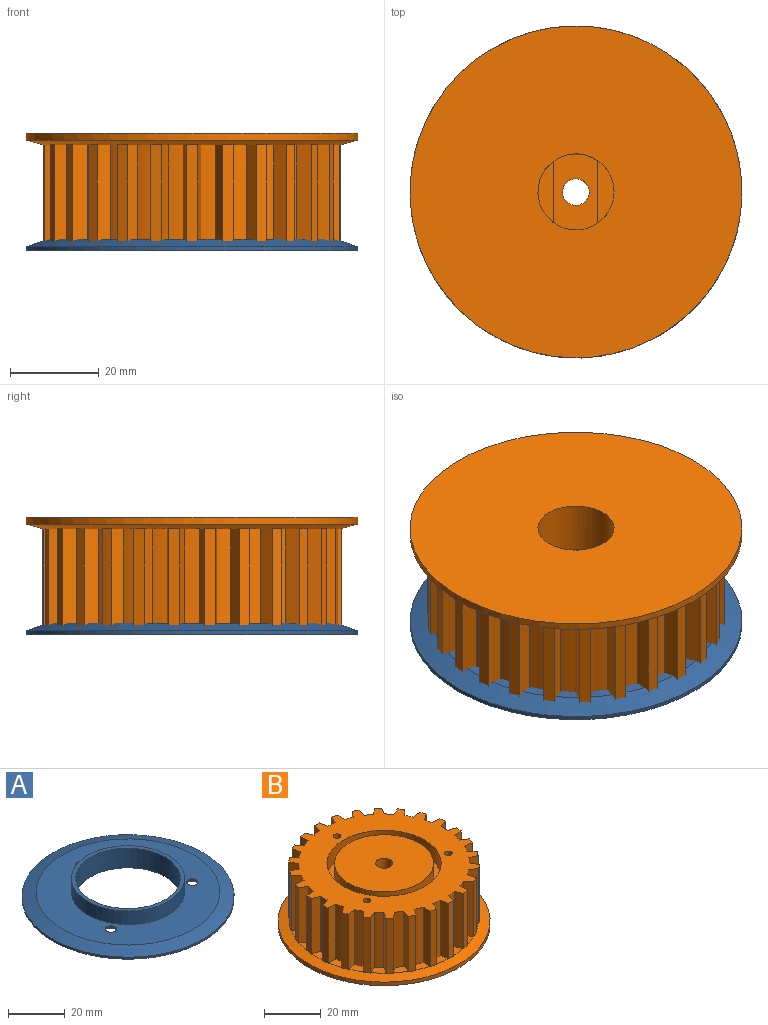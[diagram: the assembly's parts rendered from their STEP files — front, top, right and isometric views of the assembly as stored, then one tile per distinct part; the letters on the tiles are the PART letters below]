
ASSEMBLY  parts=2 mates=1
PART A: 13 faces, bbox 75x75x8.5 mm
  f0: cylinder r=2mm len=4mm, axis (0,0,-1), area 7.5mm2, adj f4,f9
  f1: cylinder r=2mm len=4mm, axis (0,0,-1), area 7.5mm2, adj f4,f11
  f2: cylinder r=2mm len=4mm, axis (0,0,-1), area 7.5mm2, adj f4,f10
  f3: cylinder r=37.5mm len=75mm, axis (0,0,-1), area 207mm2, adj f5,f12
  f4: plane 65x65mm, normal (0,0,1), area 2024mm2, adj f0,f1,f2,f7,f12
  f5: plane 75x75mm, normal (0,0,-1), area 3191.9mm2, adj f3,f6,f9,f10,f11
  f6: cylinder r=18.5mm len=37mm, axis (0,0,-1), area 988mm2, adj f5,f8
  f7: cylinder r=20mm len=40mm, axis (0,0,-1), area 741.4mm2, adj f4,f8
  f8: plane 40x40mm, normal (0,0,1), area 181.4mm2, adj f6,f7
  f9: cone r=4mm half-angle=45deg, axis (0,0,-1), area 53.3mm2, adj f0,f5
  f10: cone r=4mm half-angle=45deg, axis (0,0,-1), area 53.3mm2, adj f2,f5
  f11: cone r=4mm half-angle=45deg, axis (0,0,-1), area 53.3mm2, adj f1,f5
  f12: cone r=32.5mm half-angle=71deg, axis (0,0,-1), area 1162.9mm2, adj f3,f4
PART B: 151 faces, bbox 75x75x26.5 mm
  f0: plane 35x35mm, normal (0,0,1), area 933.8mm2, adj f136,f142
  f1: plane 14.05x3.64mm, normal (0,0,-1), area 35.8mm2, adj f137,f140
  f2: plane 75x75mm, normal (0,0,-1), area 4185.5mm2, adj f133,f137
  f3: plane 5.39x4.91mm, normal (0,0,1), area 14.5mm2, adj f99,f100,f101,f135
  f4: plane 5.34x4.19mm, normal (0,0,1), area 14.5mm2, adj f103,f104,f105,f135
  f5: plane 5.5x3.35mm, normal (0,0,1), area 14.5mm2, adj f107,f108,f109,f135
  f6: plane 5.34x4.19mm, normal (0,0,1), area 14.5mm2, adj f111,f112,f113,f135
  f7: plane 5.4x4.9mm, normal (0,0,1), area 14.5mm2, adj f115,f116,f117,f135
  f8: plane 5.44x5.33mm, normal (0,0,1), area 14.5mm2, adj f119,f120,f121,f135
  f9: plane 5.45x5.16mm, normal (0,0,1), area 14.5mm2, adj f123,f124,f125,f135
  f10: plane 5.25x4.58mm, normal (0,0,1), area 14.5mm2, adj f127,f128,f129,f135
  f11: plane 5.46x3.74mm, normal (0,0,1), area 14.5mm2, adj f28,f29,f131,f135
  f12: plane 5.46x3.74mm, normal (0,0,1), area 14.5mm2, adj f31,f32,f33,f135
  f13: plane 5.26x4.58mm, normal (0,0,1), area 14.5mm2, adj f35,f36,f37,f135
  f14: plane 5.46x5.15mm, normal (0,0,1), area 14.5mm2, adj f39,f40,f41,f135
  f15: plane 5.43x5.34mm, normal (0,0,1), area 14.5mm2, adj f43,f44,f45,f135
  f16: plane 5.39x4.91mm, normal (0,0,1), area 14.5mm2, adj f47,f48,f49,f135
  f17: plane 5.34x4.19mm, normal (0,0,1), area 14.5mm2, adj f51,f52,f53,f135
  f18: plane 5.5x3.35mm, normal (0,0,1), area 14.5mm2, adj f55,f56,f57,f135
  f19: plane 5.34x4.19mm, normal (0,0,1), area 14.5mm2, adj f59,f60,f61,f135
  f20: plane 5.4x4.9mm, normal (0,0,1), area 14.5mm2, adj f63,f64,f65,f135
  f21: plane 5.44x5.33mm, normal (0,0,1), area 14.5mm2, adj f67,f68,f69,f135
  f22: plane 5.45x5.16mm, normal (0,0,1), area 14.5mm2, adj f71,f72,f73,f135
  f23: plane 5.25x4.58mm, normal (0,0,1), area 14.5mm2, adj f75,f76,f77,f135
  f24: plane 5.46x3.74mm, normal (0,0,1), area 14.5mm2, adj f79,f80,f81,f135
  f25: plane 5.46x3.74mm, normal (0,0,1), area 14.5mm2, adj f83,f84,f85,f135
  f26: plane 5.26x4.58mm, normal (0,0,1), area 14.5mm2, adj f87,f88,f89,f135
  f27: plane 5.46x5.15mm, normal (0,0,1), area 14.5mm2, adj f91,f92,f93,f135
  f28: cylinder r=30.2mm len=23.9mm, axis (0,0,-1), area 78.6mm2, adj f11,f29,f131,f132
  f29: plane 23.95x3.51mm, normal (0.98,0.21,0), area 85.9mm2, adj f11,f28,f30,f132,f135
  f30: plane 23.95x2.51mm, normal (0.01,1,0), area 60.1mm2, adj f29,f31,f132,f135
  f31: plane 23.95x3.54mm, normal (-0.98,0.21,0), area 86.5mm2, adj f12,f30,f32,f132,f135
  f32: cylinder r=30.2mm len=23.9mm, axis (0,0,-1), area 78.6mm2, adj f12,f31,f33,f132
  f33: plane 23.95x3.23mm, normal (0.9,0.44,0), area 85.9mm2, adj f12,f32,f34,f132,f135
  f34: plane 23.95x2.44mm, normal (-0.23,0.97,0), area 60.1mm2, adj f33,f35,f132,f135
  f35: plane 23.95x3.62mm, normal (-1,-0.03,0), area 86.5mm2, adj f13,f34,f36,f132,f135
  f36: cylinder r=30.2mm len=23.9mm, axis (0,0,-1), area 78.6mm2, adj f13,f35,f37,f132
  f37: plane 23.95x2.76mm, normal (0.77,0.64,0), area 85.9mm2, adj f13,f36,f38,f132,f135
  f38: plane 23.95x2.23mm, normal (-0.45,0.89,0), area 60.1mm2, adj f37,f39,f132,f135
  f39: plane 23.95x3.48mm, normal (-0.96,-0.27,0), area 86.5mm2, adj f14,f38,f40,f132,f135
  f40: cylinder r=30.2mm len=23.9mm, axis (0,0,-1), area 78.6mm2, adj f14,f39,f41,f132
  f41: plane 23.95x2.89mm, normal (0.59,0.8,0), area 85.9mm2, adj f14,f40,f42,f132,f135
  f42: plane 23.95x1.9mm, normal (-0.65,0.76,0), area 60.1mm2, adj f41,f43,f132,f135
  f43: plane 23.95x3.15mm, normal (-0.87,-0.49,0), area 86.5mm2, adj f15,f42,f44,f132,f135
  f44: cylinder r=30.2mm len=23.9mm, axis (0,0,-1), area 78.6mm2, adj f15,f43,f45,f132
  f45: plane 23.95x3.32mm, normal (0.38,0.92,0), area 85.9mm2, adj f15,f44,f46,f132,f135
  f46: plane 23.95x2.05mm, normal (-0.82,0.58,0), area 60.1mm2, adj f45,f47,f132,f135
  f47: plane 23.95x2.63mm, normal (-0.73,-0.69,0), area 86.5mm2, adj f16,f46,f48,f132,f135
  f48: cylinder r=30.2mm len=23.9mm, axis (0,0,-1), area 78.6mm2, adj f16,f47,f49,f132
  f49: plane 23.95x3.55mm, normal (0.15,0.99,0), area 85.9mm2, adj f16,f48,f50,f132,f135
  f50: plane 23.95x2.33mm, normal (-0.93,0.37,0), area 60.1mm2, adj f49,f51,f132,f135
  f51: plane 23.95x3.05mm, normal (-0.54,-0.84,0), area 86.5mm2, adj f17,f50,f52,f132,f135
  f52: cylinder r=30.2mm len=23.9mm, axis (0,0,-1), area 78.6mm2, adj f17,f51,f53,f132
  f53: plane 23.95x3.58mm, normal (-0.09,1,0), area 85.9mm2, adj f17,f52,f54,f132,f135
  f54: plane 23.95x2.49mm, normal (-0.99,0.13,0), area 60.1mm2, adj f53,f55,f132,f135
  f55: plane 23.95x3.43mm, normal (-0.32,-0.95,0), area 86.5mm2, adj f18,f54,f56,f132,f135
  f56: cylinder r=30.2mm len=23.9mm, axis (0,0,-1), area 78.6mm2, adj f18,f55,f57,f132
  f57: plane 23.95x3.4mm, normal (-0.33,0.95,0), area 85.9mm2, adj f18,f56,f58,f132,f135
  f58: plane 23.95x2.49mm, normal (-0.99,-0.11,0), area 60.1mm2, adj f57,f59,f132,f135
  f59: plane 23.95x3.61mm, normal (-0.09,-1,0), area 86.5mm2, adj f19,f58,f60,f132,f135
  f60: cylinder r=30.2mm len=23.9mm, axis (0,0,-1), area 78.6mm2, adj f19,f59,f61,f132
  f61: plane 23.95x3.02mm, normal (-0.54,0.84,0), area 85.9mm2, adj f19,f60,f62,f132,f135
  f62: plane 23.95x2.36mm, normal (-0.94,-0.34,0), area 60.1mm2, adj f61,f63,f132,f135
  f63: plane 23.95x3.58mm, normal (0.15,-0.99,0), area 86.5mm2, adj f20,f62,f64,f132,f135
  f64: cylinder r=30.2mm len=23.9mm, axis (0,0,-1), area 78.6mm2, adj f20,f63,f65,f132
  f65: plane 23.95x2.61mm, normal (-0.73,0.69,0), area 85.9mm2, adj f20,f64,f66,f132,f135
  f66: plane 23.95x2.08mm, normal (-0.83,-0.56,0), area 60.1mm2, adj f65,f67,f132,f135
  f67: plane 23.95x3.34mm, normal (0.39,-0.92,0), area 86.5mm2, adj f21,f66,f68,f132,f135
  f68: cylinder r=30.2mm len=23.9mm, axis (0,0,-1), area 78.6mm2, adj f21,f67,f69,f132
  f69: plane 23.95x3.13mm, normal (-0.87,0.49,0), area 85.9mm2, adj f21,f68,f70,f132,f135
  f70: plane 23.95x1.86mm, normal (-0.67,-0.74,0), area 60.1mm2, adj f69,f71,f132,f135
  f71: plane 23.95x2.91mm, normal (0.6,-0.8,0), area 86.5mm2, adj f22,f70,f72,f132,f135
  f72: cylinder r=30.2mm len=23.9mm, axis (0,0,-1), area 78.6mm2, adj f22,f71,f73,f132
  f73: plane 23.95x3.46mm, normal (-0.96,0.27,0), area 85.9mm2, adj f22,f72,f74,f132,f135
  f74: plane 23.95x2.21mm, normal (-0.48,-0.88,0), area 60.1mm2, adj f73,f75,f132,f135
  f75: plane 23.95x2.79mm, normal (0.77,-0.64,0), area 86.5mm2, adj f23,f74,f76,f132,f135
  f76: cylinder r=30.2mm len=23.9mm, axis (0,0,-1), area 78.6mm2, adj f23,f75,f77,f132
  f77: plane 23.95x3.59mm, normal (-1,0.03,0), area 85.9mm2, adj f23,f76,f78,f132,f135
  f78: plane 23.95x2.43mm, normal (-0.25,-0.97,0), area 60.1mm2, adj f77,f79,f132,f135
  f79: plane 23.95x3.26mm, normal (0.9,-0.43,0), area 86.5mm2, adj f24,f78,f80,f132,f135
  f80: cylinder r=30.2mm len=23.9mm, axis (0,0,-1), area 78.6mm2, adj f24,f79,f81,f132
  f81: plane 23.95x3.51mm, normal (-0.98,-0.21,0), area 85.9mm2, adj f24,f80,f82,f132,f135
  f82: plane 23.95x2.51mm, normal (-0.01,-1,0), area 60.1mm2, adj f81,f83,f132,f135
  f83: plane 23.95x3.54mm, normal (0.98,-0.21,0), area 86.5mm2, adj f25,f82,f84,f132,f135
  f84: cylinder r=30.2mm len=23.9mm, axis (0,0,-1), area 78.6mm2, adj f25,f83,f85,f132
  f85: plane 23.95x3.23mm, normal (-0.9,-0.44,0), area 85.9mm2, adj f25,f84,f86,f132,f135
  f86: plane 23.95x2.44mm, normal (0.23,-0.97,0), area 60.1mm2, adj f85,f87,f132,f135
  f87: plane 23.95x3.62mm, normal (1,0.03,0), area 86.5mm2, adj f26,f86,f88,f132,f135
  f88: cylinder r=30.2mm len=23.9mm, axis (0,0,-1), area 78.6mm2, adj f26,f87,f89,f132
  f89: plane 23.95x2.76mm, normal (-0.77,-0.64,0), area 85.9mm2, adj f26,f88,f90,f132,f135
  f90: plane 23.95x2.23mm, normal (0.45,-0.89,0), area 60.1mm2, adj f89,f91,f132,f135
  f91: plane 23.95x3.48mm, normal (0.96,0.27,0), area 86.5mm2, adj f27,f90,f92,f132,f135
  f92: cylinder r=30.2mm len=23.9mm, axis (0,0,-1), area 78.6mm2, adj f27,f91,f93,f132
  f93: plane 23.95x2.89mm, normal (-0.59,-0.8,0), area 85.9mm2, adj f27,f92,f94,f132,f135
  f94: plane 23.95x1.9mm, normal (0.65,-0.76,0), area 60.1mm2, adj f93,f95,f132,f135
  f95: plane 23.95x3.15mm, normal (0.87,0.49,0), area 86.5mm2, adj f94,f96,f132,f134,f135
  f96: cylinder r=30.2mm len=23.9mm, axis (0,0,-1), area 78.6mm2, adj f95,f97,f132,f134
  f97: plane 23.95x3.32mm, normal (-0.38,-0.92,0), area 85.9mm2, adj f96,f98,f132,f134,f135
  f98: plane 23.95x2.05mm, normal (0.82,-0.58,0), area 60.1mm2, adj f97,f99,f132,f135
  f99: plane 23.95x2.63mm, normal (0.73,0.69,0), area 86.5mm2, adj f3,f98,f100,f132,f135
  f100: cylinder r=30.2mm len=23.9mm, axis (0,0,-1), area 78.6mm2, adj f3,f99,f101,f132
  f101: plane 23.95x3.55mm, normal (-0.15,-0.99,0), area 85.9mm2, adj f3,f100,f102,f132,f135
  f102: plane 23.95x2.33mm, normal (0.93,-0.37,0), area 60.1mm2, adj f101,f103,f132,f135
  f103: plane 23.95x3.05mm, normal (0.54,0.84,0), area 86.5mm2, adj f4,f102,f104,f132,f135
  f104: cylinder r=30.2mm len=23.9mm, axis (0,0,-1), area 78.6mm2, adj f4,f103,f105,f132
  f105: plane 23.95x3.58mm, normal (0.09,-1,0), area 85.9mm2, adj f4,f104,f106,f132,f135
  f106: plane 23.95x2.49mm, normal (0.99,-0.13,0), area 60.1mm2, adj f105,f107,f132,f135
  f107: plane 23.95x3.43mm, normal (0.32,0.95,0), area 86.5mm2, adj f5,f106,f108,f132,f135
  f108: cylinder r=30.2mm len=23.9mm, axis (0,0,-1), area 78.6mm2, adj f5,f107,f109,f132
  f109: plane 23.95x3.4mm, normal (0.33,-0.95,0), area 85.9mm2, adj f5,f108,f110,f132,f135
  f110: plane 23.95x2.49mm, normal (0.99,0.11,0), area 60.1mm2, adj f109,f111,f132,f135
  f111: plane 23.95x3.61mm, normal (0.09,1,0), area 86.5mm2, adj f6,f110,f112,f132,f135
  f112: cylinder r=30.2mm len=23.9mm, axis (0,0,-1), area 78.6mm2, adj f6,f111,f113,f132
  f113: plane 23.95x3.02mm, normal (0.54,-0.84,0), area 85.9mm2, adj f6,f112,f114,f132,f135
  f114: plane 23.95x2.36mm, normal (0.94,0.34,0), area 60.1mm2, adj f113,f115,f132,f135
  f115: plane 23.95x3.58mm, normal (-0.15,0.99,0), area 86.5mm2, adj f7,f114,f116,f132,f135
  f116: cylinder r=30.2mm len=23.9mm, axis (0,0,-1), area 78.6mm2, adj f7,f115,f117,f132
  f117: plane 23.95x2.61mm, normal (0.73,-0.69,0), area 85.9mm2, adj f7,f116,f118,f132,f135
  f118: plane 23.95x2.08mm, normal (0.83,0.56,0), area 60.1mm2, adj f117,f119,f132,f135
  f119: plane 23.95x3.34mm, normal (-0.39,0.92,0), area 86.5mm2, adj f8,f118,f120,f132,f135
  f120: cylinder r=30.2mm len=23.9mm, axis (0,0,-1), area 78.6mm2, adj f8,f119,f121,f132
  f121: plane 23.95x3.13mm, normal (0.87,-0.49,0), area 85.9mm2, adj f8,f120,f122,f132,f135
  f122: plane 23.95x1.86mm, normal (0.67,0.74,0), area 60.1mm2, adj f121,f123,f132,f135
  f123: plane 23.95x2.91mm, normal (-0.6,0.8,0), area 86.5mm2, adj f9,f122,f124,f132,f135
  f124: cylinder r=30.2mm len=23.9mm, axis (0,0,-1), area 78.6mm2, adj f9,f123,f125,f132
  f125: plane 23.95x3.46mm, normal (0.96,-0.27,0), area 85.9mm2, adj f9,f124,f126,f132,f135
  f126: plane 23.95x2.21mm, normal (0.48,0.88,0), area 60.1mm2, adj f125,f127,f132,f135
  f127: plane 23.95x2.79mm, normal (-0.77,0.64,0), area 86.5mm2, adj f10,f126,f128,f132,f135
  f128: cylinder r=30.2mm len=23.9mm, axis (0,0,-1), area 78.6mm2, adj f10,f127,f129,f132
  f129: plane 23.95x3.59mm, normal (1,-0.03,0), area 85.9mm2, adj f10,f128,f130,f132,f135
  f130: plane 23.95x2.43mm, normal (0.25,0.97,0), area 60.1mm2, adj f129,f131,f132,f135
  f131: plane 23.95x3.26mm, normal (-0.9,0.43,0), area 86.5mm2, adj f11,f28,f130,f132,f135
  f132: plane 67.35x67.17mm, normal (0,0,1), area 1860.3mm2, adj f28,f29,f30,f31,f32,f33,f34,f35
  f133: cylinder r=37.5mm len=75mm, axis (0,0,-1), area 360.1mm2, adj f2,f135
  f134: plane 5.43x5.34mm, normal (0,0,1), area 14.5mm2, adj f95,f96,f97,f135
  f135: cone r=33.5mm half-angle=75deg, axis (0,0,-1), area 912.1mm2, adj f3,f4,f5,f6,f7,f8,f9,f10
  f136: cylinder r=3mm len=6.5mm, axis (0,0,-1), area 122.5mm2, adj f0,f141
  f137: cylinder r=8.6mm len=20mm, axis (0,0,-1), area 819.2mm2, adj f1,f2,f138,f139,f140,f141
  f138: plane 13.94x3.56mm, normal (0,0,-1), area 34.8mm2, adj f137,f139
  f139: plane 13.94x8mm, normal (1,0,0), area 111.5mm2, adj f137,f138,f141
  f140: plane 14.05x8mm, normal (-1,0,0), area 112.4mm2, adj f1,f137,f141
  f141: plane 17.2x10mm, normal (0,0,-1), area 133.5mm2, adj f136,f137,f139,f140
  f142: cylinder r=17.5mm len=35mm, axis (0,0,1), area 714.7mm2, adj f0,f144
  f143: cylinder r=20.2mm len=40.4mm, axis (0,0,1), area 825mm2, adj f132,f144
  f144: plane 40.4x40.4mm, normal (0,0,1), area 319.8mm2, adj f142,f143
  f145: cylinder r=1.35mm len=10mm, axis (0,0,1), area 84.8mm2, adj f132,f146
  f146: plane 2.7x2.7mm, normal (0,0,1), area 5.7mm2, adj f145
  f147: cylinder r=1.35mm len=10mm, axis (0,0,1), area 84.8mm2, adj f132,f148
  f148: plane 2.7x2.7mm, normal (0,0,1), area 5.7mm2, adj f147
  f149: cylinder r=1.35mm len=10mm, axis (0,0,1), area 84.8mm2, adj f132,f150
  f150: plane 2.7x2.7mm, normal (0,0,1), area 5.7mm2, adj f149
PLACE A rot(axis=(0,0,1),60.1deg) t=(94.92,-32.92,11.07)mm
PLACE B rot(axis=(1,0,0),180deg) t=(94.92,-32.92,37.57)mm fixed
MATE revolute B.f142 <-> A.f6  axis (0,0,-1) through (94.92,-32.92,11.07)mm
